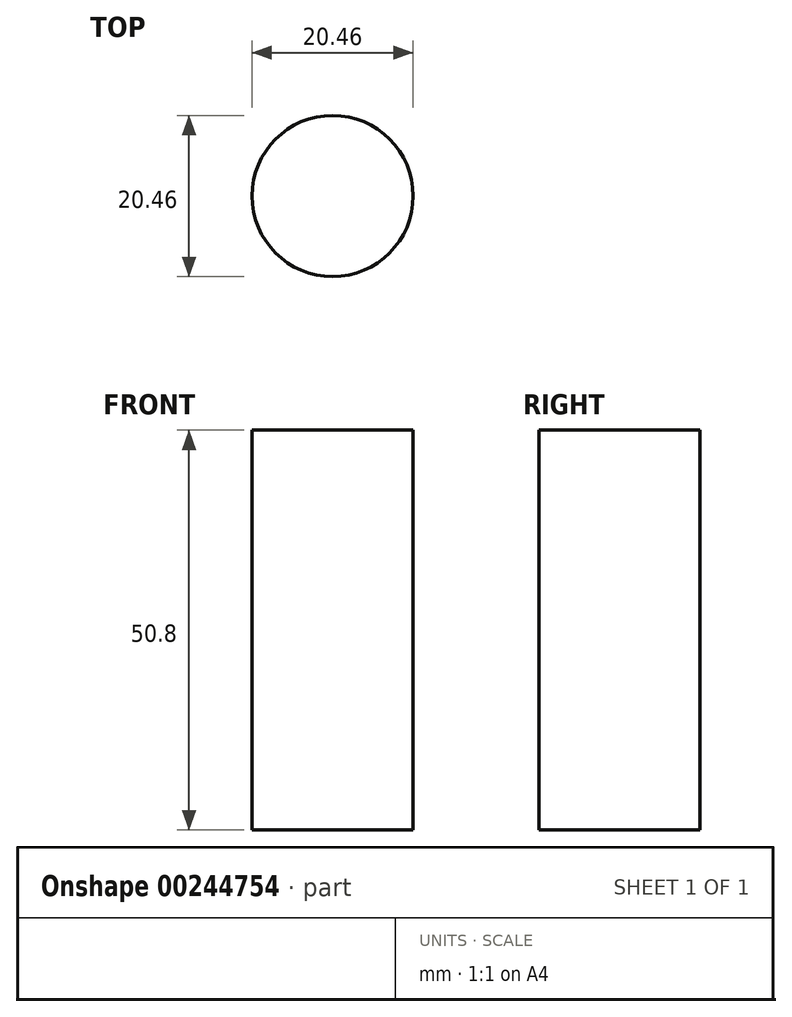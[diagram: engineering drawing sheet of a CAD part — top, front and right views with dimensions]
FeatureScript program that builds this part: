
annotation { "Feature Type Name" : "Feature", "Feature Type Description" : "" }
export const myFeature = defineFeature(function(context is Context, id is Id, definition is map)
    precondition{}
    {
        {
            var Q0;
            Q0=qCreatedBy(makeId("Top.planeOp"),FACE);
            var sketch = newSketch(context, id + "F0", { "sketchPlane" : qUnion([Q0])});
            skCircle(sketch, "E0", {"center": v(0, 0) * mm, "radius": 10.23 * mm});
            skSolve(sketch);
        }
        {
            var Q0;
            Q0=makeQuery(id+"F0.imprint","IMPRINT",FACE,{"disambiguationData":[TD([[makeQuery(id+"F0.imprint","IMPRINT",EDGE,{"derivedFrom":sQuery(id+"F0.wireOp",EDGE,"E0")}),1.0]])]});
            extrude(context, id + "F1", {"entities" : qUnion([Q0]), "depth" : 50.8 * mm});
        }
    });
